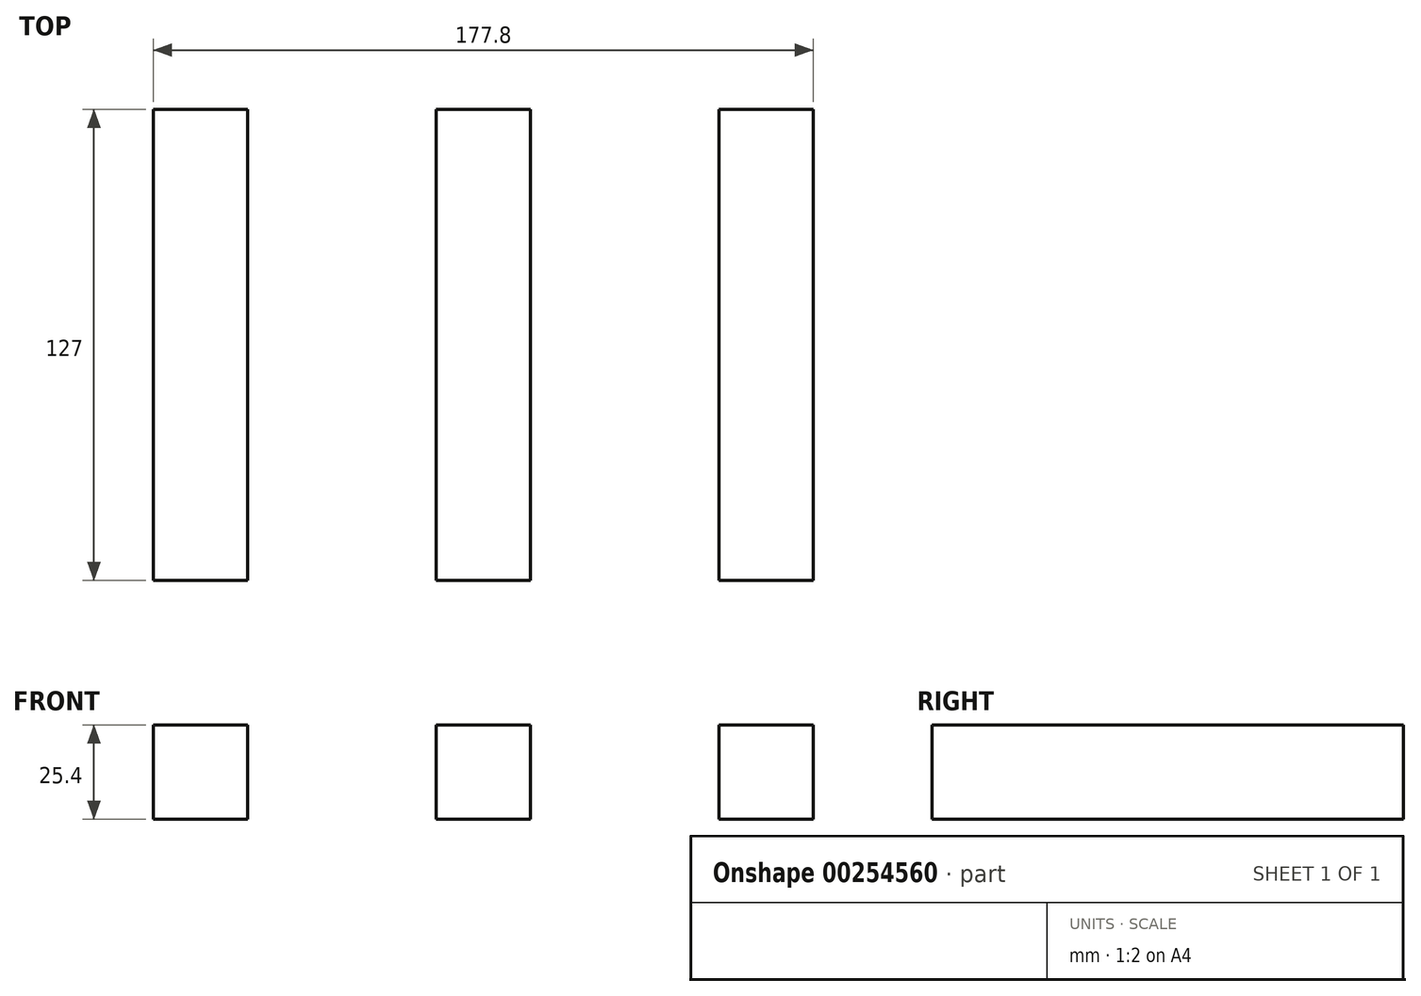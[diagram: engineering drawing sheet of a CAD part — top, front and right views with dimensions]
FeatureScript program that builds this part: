
annotation { "Feature Type Name" : "Feature", "Feature Type Description" : "" }
export const myFeature = defineFeature(function(context is Context, id is Id, definition is map)
    precondition{}
    {
        {
            var Q0;
            Q0=qCreatedBy(makeId("Front.planeOp"),FACE);
            var sketch = newSketch(context, id + "F0", { "sketchPlane" : qUnion([Q0])});
            skLineSegment(sketch, "E0.bottom", {"start": v(-68.56, 28.96) * mm, "end": v(-43.16, 28.96) * mm});
            skLineSegment(sketch, "E0.top", {"start": v(-68.56, 3.56) * mm, "end": v(-43.16, 3.56) * mm});
            skLineSegment(sketch, "E0.left", {"start": v(-68.56, 28.96) * mm, "end": v(-68.56, 3.56) * mm});
            skLineSegment(sketch, "E0.right", {"start": v(-43.16, 28.96) * mm, "end": v(-43.16, 3.56) * mm});
            skLineSegment(sketch, "E1", {"start": v(-43.16, 3.56) * mm, "end": v(7.64, 3.56) * mm});
            skLineSegment(sketch, "E2.bottom", {"start": v(7.64, 3.56) * mm, "end": v(33.04, 3.56) * mm});
            skLineSegment(sketch, "E2.top", {"start": v(7.64, 28.96) * mm, "end": v(33.04, 28.96) * mm});
            skLineSegment(sketch, "E2.left", {"start": v(7.64, 3.56) * mm, "end": v(7.64, 28.96) * mm});
            skLineSegment(sketch, "E2.right", {"start": v(33.04, 3.56) * mm, "end": v(33.04, 28.96) * mm});
            skLineSegment(sketch, "E3", {"start": v(33.04, 3.56) * mm, "end": v(83.84, 3.56) * mm});
            skLineSegment(sketch, "E4.bottom", {"start": v(83.84, 3.56) * mm, "end": v(109.24, 3.56) * mm});
            skLineSegment(sketch, "E4.top", {"start": v(83.84, 28.96) * mm, "end": v(109.24, 28.96) * mm});
            skLineSegment(sketch, "E4.left", {"start": v(83.84, 3.56) * mm, "end": v(83.84, 28.96) * mm});
            skLineSegment(sketch, "E4.right", {"start": v(109.24, 3.56) * mm, "end": v(109.24, 28.96) * mm});
            skSolve(sketch);
        }
        {
            var Q0;
            Q0 = qSketchRegion(id + "F0", true);
            extrude(context, id + "F1", {"entities" : qUnion([Q0]), "endBound" : BoundingType.SYMMETRIC, "depth" : 127 * mm});
        }
    });
